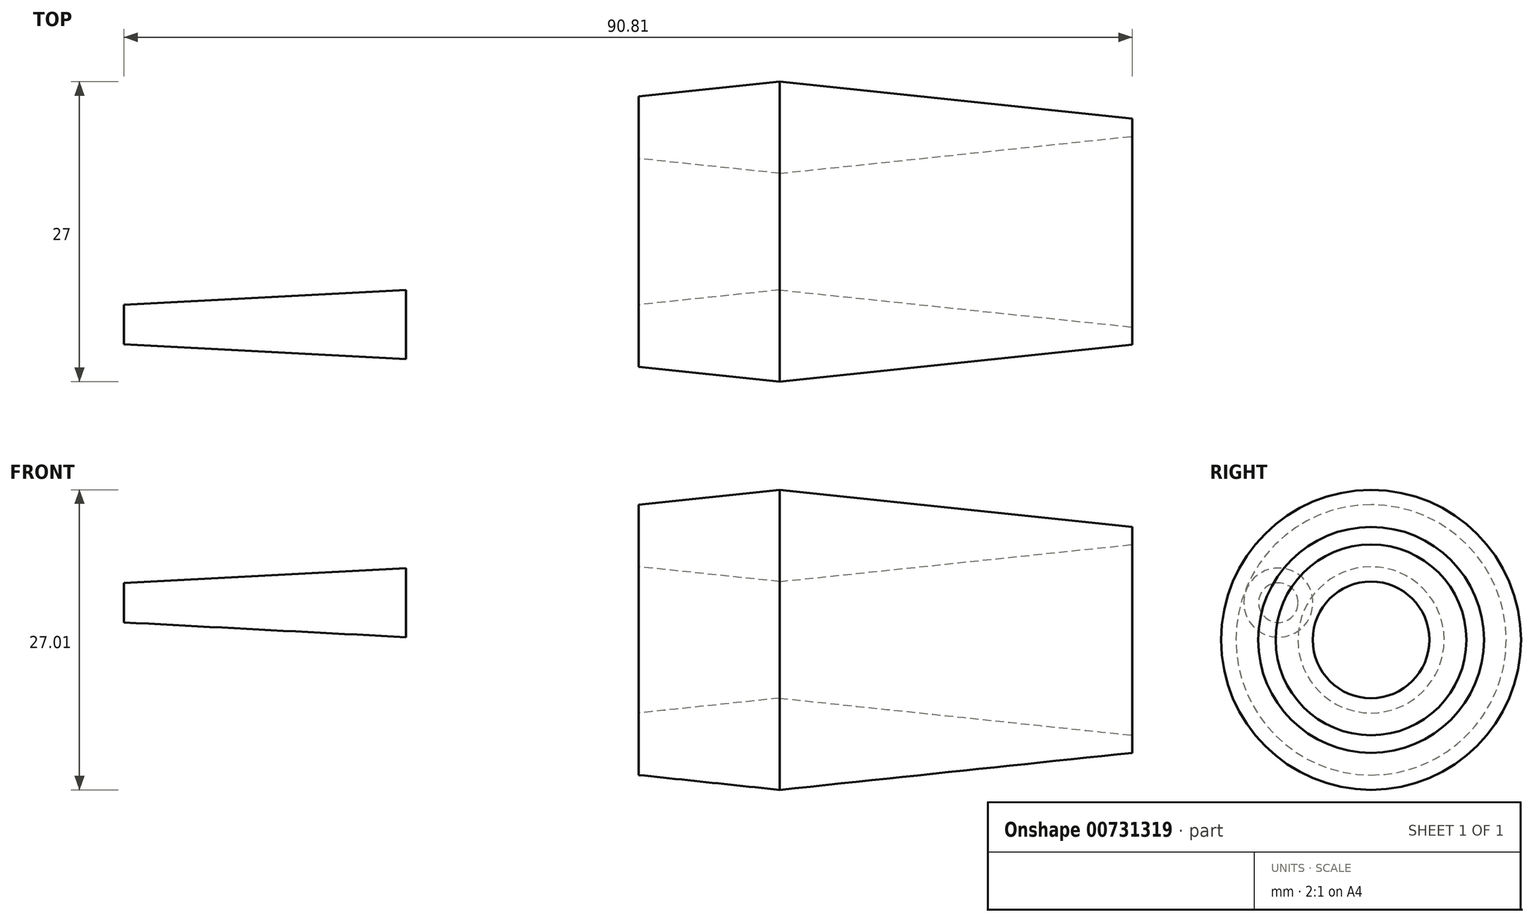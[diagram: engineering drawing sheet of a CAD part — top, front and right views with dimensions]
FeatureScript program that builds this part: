
annotation { "Feature Type Name" : "Feature", "Feature Type Description" : "" }
export const myFeature = defineFeature(function(context is Context, id is Id, definition is map)
    precondition{}
    {
        {
            var Q0;
            Q0=qCreatedBy(makeId("Front.planeOp"),FACE);
            var sketch = newSketch(context, id + "F0", { "sketchPlane" : qUnion([Q0])});
            skLineSegment(sketch, "E0", {"start": v(-45.33, 12.56) * mm, "end": v(39.87, 12.56) * mm});
            skArc(sketch, "E1", {"start": v(39.87, 12.56) * mm, "mid": v(34.28, 20.58) * mm, "end": v(24.94, 23.48) * mm});
            skArc(sketch, "E2", {"start": v(8.56, 18.02) * mm, "mid": v(17.62, 18.13) * mm, "end": v(24.94, 23.48) * mm});
            skArc(sketch, "E3", {"start": v(0, 15.3) * mm, "mid": v(4.5, 15.98) * mm, "end": v(8.56, 18.02) * mm});
            skSolve(sketch);
        }
        {
            var Q0;
            Q0=sQuery(id+"F0.wireOp",EDGE,"E3");
            var Q1;
            Q1=sQuery(id+"F0.wireOp",EDGE,"E2");
            var Q2;
            Q2=sQuery(id+"F0.wireOp",EDGE,"E1");
            var Q3;
            Q3=sQuery(id+"F0.wireOp",EDGE,"E0");
            revolve(context, id + "F1", {"bodyType" : ToolBodyType.SURFACE, "surfaceOperationType" : NewSurfaceOperationType.NEW, "surfaceEntities" : qUnion([Q0, Q1, Q2]), "axis" : qUnion([Q3]), "revolveType" : RevolveType.FULL});
        }
        {
            var Q0;
            Q0=qCreatedBy(makeId("Front.planeOp"),FACE);
            var sketch = newSketch(context, id + "F2", { "sketchPlane" : qUnion([Q0])});
            skLineSegment(sketch, "E4", {"start": v(-69.97, 17.03) * mm, "end": v(-57.27, 17.03) * mm});
            skLineSegment(sketch, "E5", {"start": v(-57.27, 17.03) * mm, "end": v(-57.27, 25.29) * mm});
            skLineSegment(sketch, "E6", {"start": v(-57.27, 25.29) * mm, "end": v(-50.92, 25.29) * mm});
            skLineSegment(sketch, "E7", {"start": v(-50.92, 25.29) * mm, "end": v(-50.92, 17.03) * mm});
            skLineSegment(sketch, "E8", {"start": v(-50.92, 17.03) * mm, "end": v(-31.87, 17.03) * mm});
            skLineSegment(sketch, "E9", {"start": v(-31.87, 17.03) * mm, "end": v(-31.87, 25.29) * mm});
            skLineSegment(sketch, "E10", {"start": v(-31.87, 25.29) * mm, "end": v(-23.61, 25.29) * mm});
            skLineSegment(sketch, "E11", {"start": v(-23.61, 25.29) * mm, "end": v(-23.61, 17.03) * mm});
            skLineSegment(sketch, "E12", {"start": v(-73.02, 11.78) * mm, "end": v(-9.52, 11.78) * mm});
            skSolve(sketch);
        }
        {
            var Q0;
            Q0=sQuery(id+"F2.wireOp",EDGE,"E6");
            var Q1;
            Q1=sQuery(id+"F2.wireOp",EDGE,"E10");
            var Q2;
            Q2=sQuery(id+"F2.wireOp",EDGE,"E11");
            var Q3;
            Q3=sQuery(id+"F2.wireOp",EDGE,"E7");
            var Q4;
            Q4=sQuery(id+"F2.wireOp",EDGE,"E9");
            var Q5;
            Q5=sQuery(id+"F2.wireOp",EDGE,"E8");
            var Q6;
            Q6=sQuery(id+"F2.wireOp",EDGE,"E5");
            var Q7;
            Q7=sQuery(id+"F2.wireOp",EDGE,"E4");
            var Q8;
            Q8=sQuery(id+"F2.wireOp",EDGE,"E12");
            revolve(context, id + "F3", {"bodyType" : ToolBodyType.SURFACE, "surfaceOperationType" : NewSurfaceOperationType.NEW, "surfaceEntities" : qUnion([Q0, Q1, Q2, Q3, Q4, Q5, Q6, Q7]), "axis" : qUnion([Q8]), "revolveType" : RevolveType.FULL});
        }
        {
            var Q0;
            Q0=makeQuery(id+"F3.opRevolve","SWEPT_FACE",FACE,{"disambiguationData":[OSD([sQuery(id+"F2.wireOp",EDGE,"E11")])]});
            extrude(context, id + "F4", {"entities" : qUnion([Q0]), "oppositeDirection" : true, "depth" : 31.75 * mm, "offsetDistance" : 25.4 * mm, "hasDraft" : true, "draftAngle" : 6 * degree, "draftPullDirection" : true, "hasSecondDirection" : true, "secondDirectionOppositeDirection" : false, "secondDirectionDepth" : 12.7 * mm, "hasSecondDirectionDraft" : true, "secondDirectionDraftAngle" : 6 * degree, "secondDirectionDraftPullDirection" : true});
        }
        {
            var Q0;
            Q0=makeQuery(id+"F3.opRevolve","SWEPT_FACE",FACE,{"disambiguationData":[OSD([sQuery(id+"F2.wireOp",EDGE,"E5")])]});
            var sketch = newSketch(context, id + "F5", { "sketchPlane" : qUnion([Q0])});
            skCircle(sketch, "E13", {"center": v(-8.35, 15.13) * mm, "radius": 3.11 * mm});
            skSolve(sketch);
        }
        {
            var Q0;
            Q0=makeQuery(id+"F5.imprint","IMPRINT",FACE,{"disambiguationData":[TD([[makeQuery(id+"F5.imprint","IMPRINT",EDGE,{"derivedFrom":sQuery(id+"F5.wireOp",EDGE,"E13")}),1.0]])]});
            extrude(context, id + "F6", {"entities" : qUnion([Q0]), "oppositeDirection" : true, "depth" : 25.4 * mm, "offsetDistance" : 25.4 * mm, "hasDraft" : true, "draftAngle" : 3 * degree, "draftPullDirection" : true});
        }
    });
